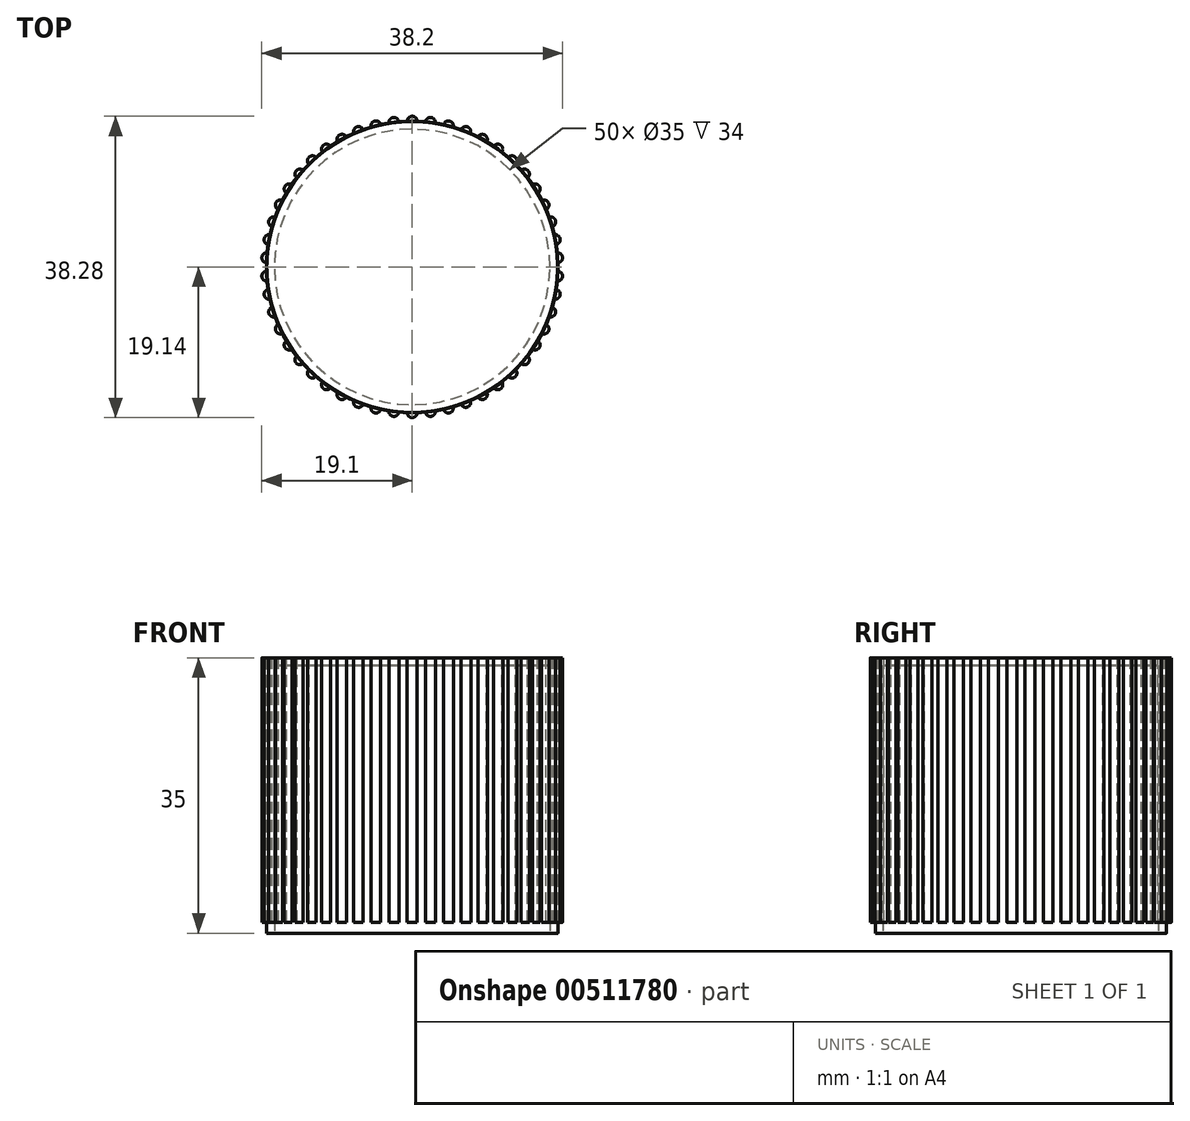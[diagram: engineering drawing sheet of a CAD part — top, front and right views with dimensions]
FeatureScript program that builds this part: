
annotation { "Feature Type Name" : "Feature", "Feature Type Description" : "" }
export const myFeature = defineFeature(function(context is Context, id is Id, definition is map)
    precondition{}
    {
        {
            var Q0;
            Q0=qCreatedBy(makeId("Top.planeOp"),FACE);
            var sketch = newSketch(context, id + "F0", { "sketchPlane" : qUnion([Q0])});
            skCircle(sketch, "E0", {"center": v(0, 0) * mm, "radius": 18.5 * mm});
            skSolve(sketch);
        }
        {
            var Q0;
            Q0=makeQuery(id+"F0.imprint","IMPRINT",FACE,{"disambiguationData":[TD([[makeQuery(id+"F0.imprint","IMPRINT",EDGE,{"derivedFrom":sQuery(id+"F0.wireOp",EDGE,"E0")}),1.0]])]});
            extrude(context, id + "F1", {"entities" : qUnion([Q0]), "depth" : 35 * mm});
        }
        {
            var Q0;
            Q0=makeQuery(id+"F1.opExtrude","CAP_FACE",FACE,{"disambiguationData":[OSD([sQuery(id+"F0.wireOp",EDGE,"E0")])],"isStart":true});
            shell(context, id + "F2", {"entities" : qUnion([Q0]), "thickness" : 1 * mm});
        }
        {
            var Q0;
            Q0=makeQuery(id+"F1.opExtrude","CAP_FACE",FACE,{"disambiguationData":[OSD([sQuery(id+"F0.wireOp",EDGE,"E0")])],"isStart":false});
            var sketch = newSketch(context, id + "F3", { "sketchPlane" : qUnion([Q0])});
            skCircle(sketch, "E1", {"center": v(0, 18.5) * mm, "radius": 0.64 * mm});
            skSolve(sketch);
        }
        {
            var Q0;
            {var subQ0=sQuery(id+"F3.wireOp",EDGE,"E1");var subQ1=makeQuery(id+"F1.opExtrude","CAP_EDGE",EDGE,{"disambiguationData":[OSD([sQuery(id+"F0.wireOp",EDGE,"E0")])],"isStart":false});var subQ2=makeQuery(id+"F3.imprint","INTERSECT",VERTEX,{"disambiguationData":[OD(0.0)],"derivedFrom":[subQ1,subQ0]});Q0=makeQuery(id+"F3.imprint","IMPRINT",FACE,{"disambiguationData":[TD([[makeQuery(id+"F3.imprint","IMPRINT",EDGE,{"disambiguationData":[TD([[subQ2,1.0]])],"derivedFrom":subQ0}),1.0]])]});}
            extrude(context, id + "F4", {"entities" : qUnion([Q0]), "operationType" : NewBodyOperationType.ADD, "oppositeDirection" : true, "depth" : 33.6 * mm});
        }
        {
            var Q0;
            Q0=makeQuery(id+"F1.opExtrude","SWEPT_BODY",BODY,{"disambiguationData":[OSD([sQuery(id+"F0.wireOp",EDGE,"E0")])]});
            var Q1;
            Q1=makeQuery(id+"F1.opExtrude","CAP_EDGE",EDGE,{"disambiguationData":[OSD([sQuery(id+"F0.wireOp",EDGE,"E0")])],"isStart":true});
            circularPattern(context, id + "F5", {"entities" : qUnion([Q0]), "axis" : qUnion([Q1]), "angle" : 360 * degree, "instanceCount" : 50, "equalSpace" : true});
        }
    });
